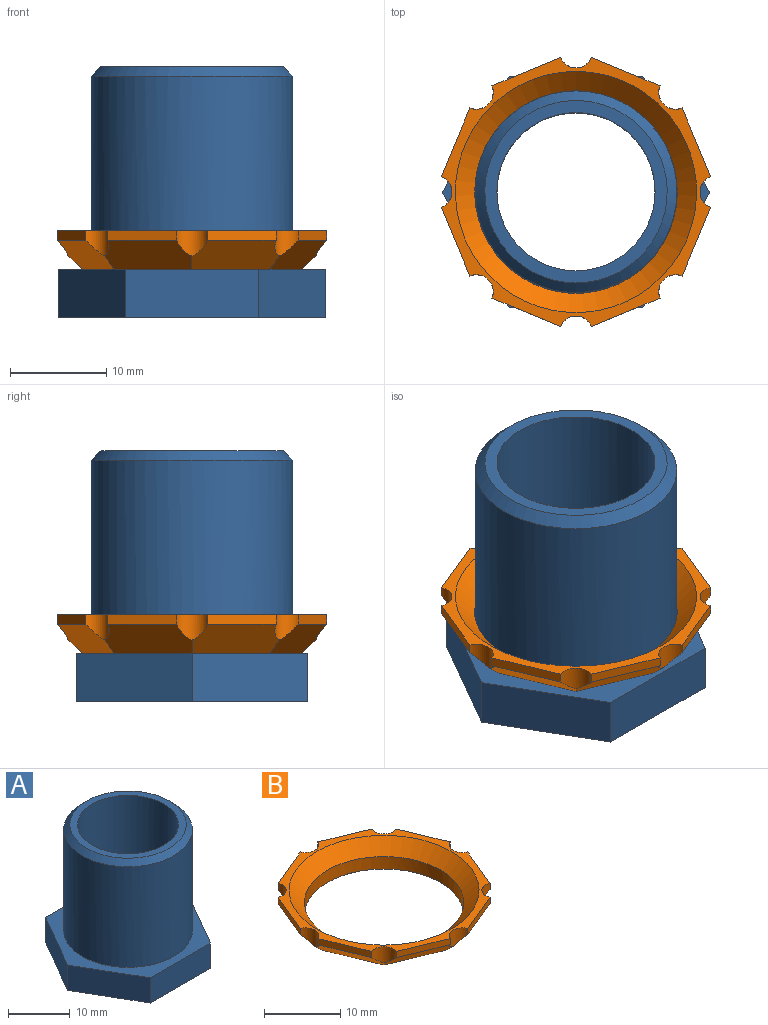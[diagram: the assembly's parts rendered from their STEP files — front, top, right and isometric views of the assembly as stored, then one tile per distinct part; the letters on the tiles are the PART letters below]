
ASSEMBLY  parts=2 mates=1
PART A: 12 faces, bbox 27.7x24x26 mm
  f0: cone r=9.45mm half-angle=45deg, axis (0,0,-1), area 88.4mm2, adj f2,f11
  f1: cylinder r=8.2mm len=26mm, axis (0,0,-1), area 1339.6mm2, adj f9,f11
  f2: cylinder r=10.45mm len=20.9mm, axis (0,0,-1), area 1313.2mm2, adj f0,f10
  f3: plane 13.86x5mm, normal (0,-1,0), area 69.3mm2, adj f4,f8,f9,f10
  f4: plane 12x6.93mm, normal (-0.87,-0.5,0), area 69.3mm2, adj f3,f5,f9,f10
  f5: plane 12x6.93mm, normal (-0.87,0.5,0), area 69.3mm2, adj f4,f6,f9,f10
  f6: plane 13.86x5mm, normal (0,1,0), area 69.3mm2, adj f5,f7,f9,f10
  f7: plane 12x6.93mm, normal (0.87,0.5,0), area 69.3mm2, adj f6,f8,f9,f10
  f8: plane 12x6.93mm, normal (0.87,-0.5,0), area 69.3mm2, adj f3,f7,f9,f10
  f9: plane 27.71x24mm, normal (0,0,-1), area 287.6mm2, adj f1,f3,f4,f5,f6,f7,f8
  f10: plane 27.71x24mm, normal (0,0,1), area 155.8mm2, adj f2,f3,f4,f5,f6,f7,f8
  f11: plane 18.9x18.9mm, normal (0,0,1), area 69.3mm2, adj f0,f1
PART B: 35 faces, bbox 27.9x27.9x4 mm
  f0: cone r=12.5mm half-angle=45deg, axis (0,0,1), area 204.4mm2, adj f1,f21
  f1: cylinder r=10.5mm len=21mm, axis (0,0,-1), area 131.9mm2, adj f0,f5,f6,f7,f8,f9,f10,f11
  f2: cylinder r=1.75mm len=2.62mm, axis (0,0,1), area 7.9mm2, adj f14,f15,f21,f22,f24
  f3: cylinder r=1.75mm len=2.62mm, axis (0,0,1), area 7.9mm2, adj f16,f17,f21,f23,f25
  f4: cylinder r=1.75mm len=3.23mm, axis (0,0,1), area 7.9mm2, adj f15,f16,f21,f22,f23
  f5: plane 5.68x5.68mm, normal (0,0,-1), area 2.4mm2, adj f1,f23,f25
  f6: plane 8.04x1.66mm, normal (0,0,-1), area 2.4mm2, adj f1,f25,f27
  f7: plane 5.68x5.68mm, normal (0,0,-1), area 2.4mm2, adj f1,f27,f29
  f8: plane 8.04x1.66mm, normal (0,0,-1), area 2.4mm2, adj f1,f28,f29
  f9: plane 5.68x5.68mm, normal (0,0,-1), area 2.4mm2, adj f1,f26,f28
  f10: plane 8.04x1.66mm, normal (0,0,-1), area 2.4mm2, adj f1,f24,f26
  f11: plane 5.68x5.68mm, normal (0,0,-1), area 2.4mm2, adj f1,f22,f24
  f12: plane 7.1x2.94mm, normal (-0.38,-0.92,0), area 7.7mm2, adj f21,f28,f30,f32
  f13: plane 7.1x2.94mm, normal (-0.92,-0.38,0), area 7.7mm2, adj f21,f26,f32,f34
  f14: plane 7.1x2.94mm, normal (-0.92,0.38,0), area 7.7mm2, adj f2,f21,f24,f34
  f15: plane 7.1x2.94mm, normal (-0.38,0.92,0), area 7.7mm2, adj f2,f4,f21,f22
  f16: plane 7.1x2.94mm, normal (0.38,0.92,0), area 7.7mm2, adj f3,f4,f21,f23
  f17: plane 7.1x2.94mm, normal (0.92,0.38,0), area 7.7mm2, adj f3,f21,f25,f33
  f18: plane 7.1x2.94mm, normal (0.92,-0.38,0), area 7.7mm2, adj f21,f27,f31,f33
  f19: plane 7.1x2.94mm, normal (0.38,-0.92,0), area 7.7mm2, adj f21,f29,f30,f31
  f20: plane 8.04x1.66mm, normal (0,0,-1), area 2.4mm2, adj f1,f22,f23
  f21: plane 27.89x27.89mm, normal (0,0,1), area 84.2mm2, adj f0,f2,f3,f4,f12,f13,f14,f15
  f22: plane 9.1x5.91mm, normal (-0.27,0.65,-0.71), area 37.1mm2, adj f2,f4,f11,f15,f20,f23,f24
  f23: plane 9.1x5.91mm, normal (0.27,0.65,-0.71), area 37.1mm2, adj f3,f4,f5,f16,f20,f22,f25
  f24: plane 9.11x5.92mm, normal (-0.65,0.27,-0.71), area 37.1mm2, adj f2,f10,f11,f14,f22,f26,f34
  f25: plane 9.11x5.92mm, normal (0.65,0.27,-0.71), area 37.1mm2, adj f3,f5,f6,f17,f23,f27,f33
  f26: plane 9.1x5.91mm, normal (-0.65,-0.27,-0.71), area 37.1mm2, adj f9,f10,f13,f24,f28,f32,f34
  f27: plane 9.1x5.91mm, normal (0.65,-0.27,-0.71), area 37.1mm2, adj f6,f7,f18,f25,f29,f31,f33
  f28: plane 9.1x5.91mm, normal (-0.27,-0.65,-0.71), area 37.1mm2, adj f8,f9,f12,f26,f29,f30,f32
  f29: plane 9.1x5.91mm, normal (0.27,-0.65,-0.71), area 37.1mm2, adj f7,f8,f19,f27,f28,f30,f31
  f30: cylinder r=1.75mm len=3.23mm, axis (0,0,1), area 7.9mm2, adj f12,f19,f21,f28,f29
  f31: cylinder r=1.75mm len=2.62mm, axis (0,0,1), area 7.9mm2, adj f18,f19,f21,f27,f29
  f32: cylinder r=1.75mm len=2.62mm, axis (0,0,1), area 7.9mm2, adj f12,f13,f21,f26,f28
  f33: cylinder r=1.75mm len=3.23mm, axis (0,0,1), area 7.9mm2, adj f17,f18,f21,f25,f27
  f34: cylinder r=1.75mm len=3.23mm, axis (0,0,1), area 7.9mm2, adj f13,f14,f21,f24,f26
PLACE A t=(0,0,12)mm
PLACE B t=(0,0,12)mm
MATE fastened A.f0 <-> B.f0  axis (0,0,-1) through (0,0,5)mm
